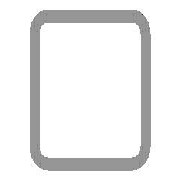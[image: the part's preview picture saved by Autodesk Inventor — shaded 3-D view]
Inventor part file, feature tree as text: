
AUTODESK INVENTOR PART (.ipt)
format: ipt  version: 2025.1 (Build 291241000, 241)  size: 188,928 bytes
history: native  units: mm (DEFAULTED — no unit token found)
features: other x9, sketch x3, extrude x2, plane x1
ambient origin geometry x8: Origin, YZ Plane, XZ Plane, XY Plane, X Axis, Y Axis, Z Axis, Center Point
bodies: Solid1 (feature_tree)
feature tree (15):
  parser-record x1  (decoder bookkeeping rows leaked as tree rows — omitted from the tree; the rows remain in map.json)
  other  "Driven Length"
  other  "Płaszczyzna początkowa"
  other  "Płaszczyzna końcowa"
  extrude  "Bryła"  TaperAngle=0.0deg  [1 undecoded]
  other  "Płaszczyzna konstrukcyjna4"
  other  "Płaszczyzna konstrukcyjna5"
  other  "Płaszczyzna konstrukcyjna6"
  extrude  "Wyciągnięcie proste2"  Depth=4.0mm
  other  "Utwórz kombinację1"
  sketch  "Sketch3"  dims[d3=800.0mm d4=0.0mm]
  plane  "Work Plane3"
  sketch  "Sketch4"  dims[d7=4.0mm d10=40.0mm d11=40.0mm d12=3.2mm d13=-0.0mm d14=800.0mm d15=20.0mm d16=20.0mm d17=90.0deg d18=800.0mm d19=0.13mm d20=0.0mm]
  sketch  "Szkic5"
  other  "Bryła2"
note: 1 required parameter value undecoded (feature->parameter linkage not recoverable at this tier; creation-order binding heuristic only, values carry confidence <= 0.55)
